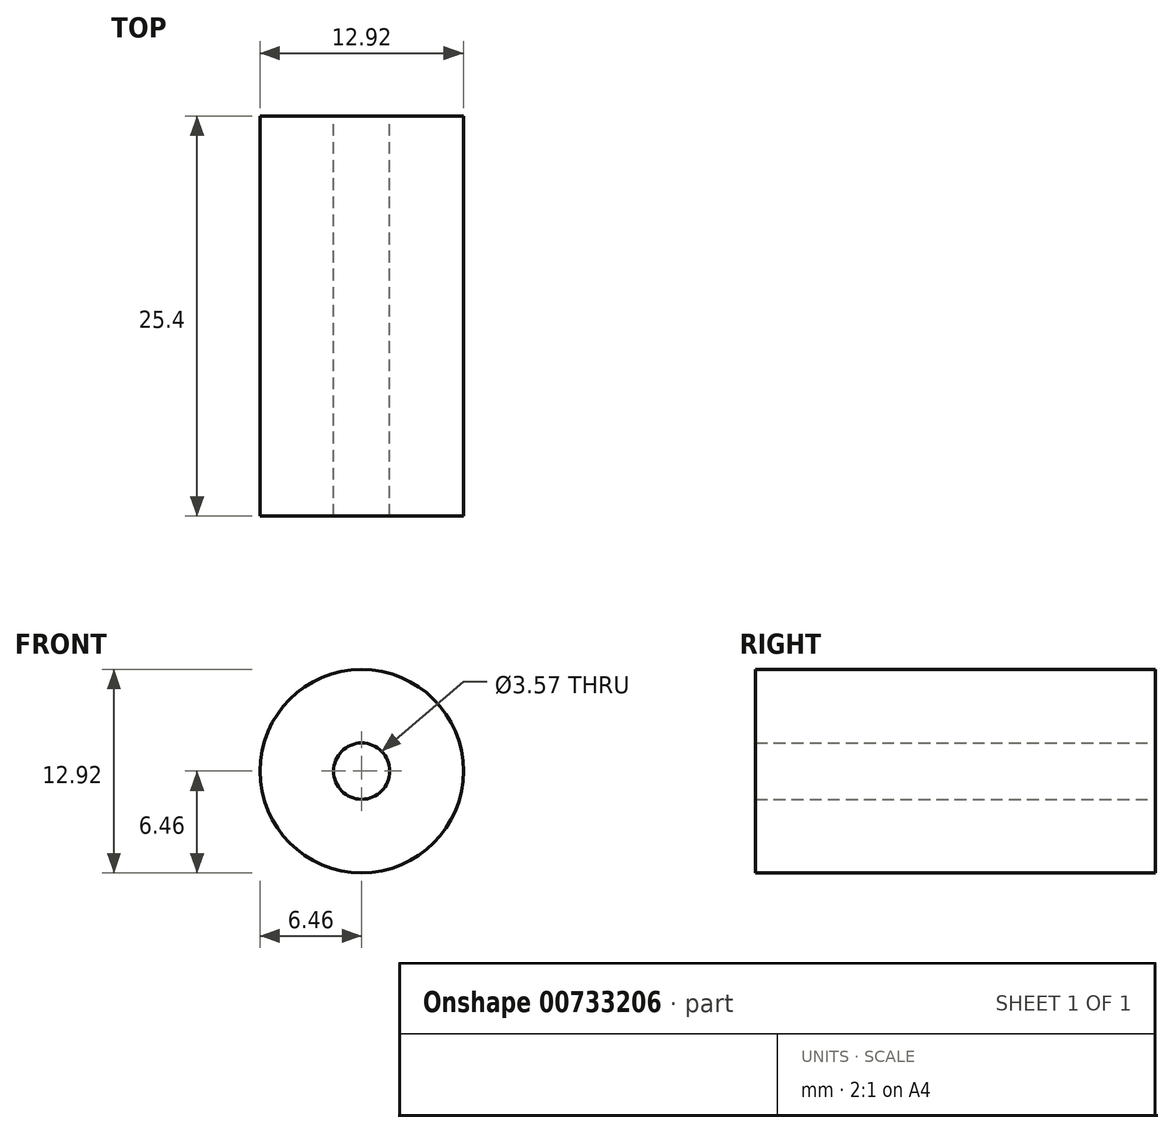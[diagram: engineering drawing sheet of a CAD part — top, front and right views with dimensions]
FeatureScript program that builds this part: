
annotation { "Feature Type Name" : "Feature", "Feature Type Description" : "" }
export const myFeature = defineFeature(function(context is Context, id is Id, definition is map)
    precondition{}
    {
        {
            var Q0;
            Q0=qCreatedBy(makeId("Front.planeOp"),FACE);
            var sketch = newSketch(context, id + "F0", { "sketchPlane" : qUnion([Q0])});
            skCircle(sketch, "E0", {"center": v(0, 0) * mm, "radius": 1.79 * mm});
            skLineSegment(sketch, "E1", {"start": v(0, -1.79) * mm, "end": v(0, -6.46) * mm});
            skCircle(sketch, "E2", {"center": v(0, 0) * mm, "radius": 6.46 * mm});
            skSolve(sketch);
        }
        {
            var Q0;
            Q0=makeQuery(id+"F0.imprint","IMPRINT",FACE,{"disambiguationData":[TD([[makeQuery(id+"F0.imprint","IMPRINT",EDGE,{"derivedFrom":sQuery(id+"F0.wireOp",EDGE,"E0")}),-1.0]])]});
            extrude(context, id + "F1", {"entities" : qUnion([Q0]), "depth" : 25.4 * mm, "offsetDistance" : 25.4 * mm});
        }
    });
